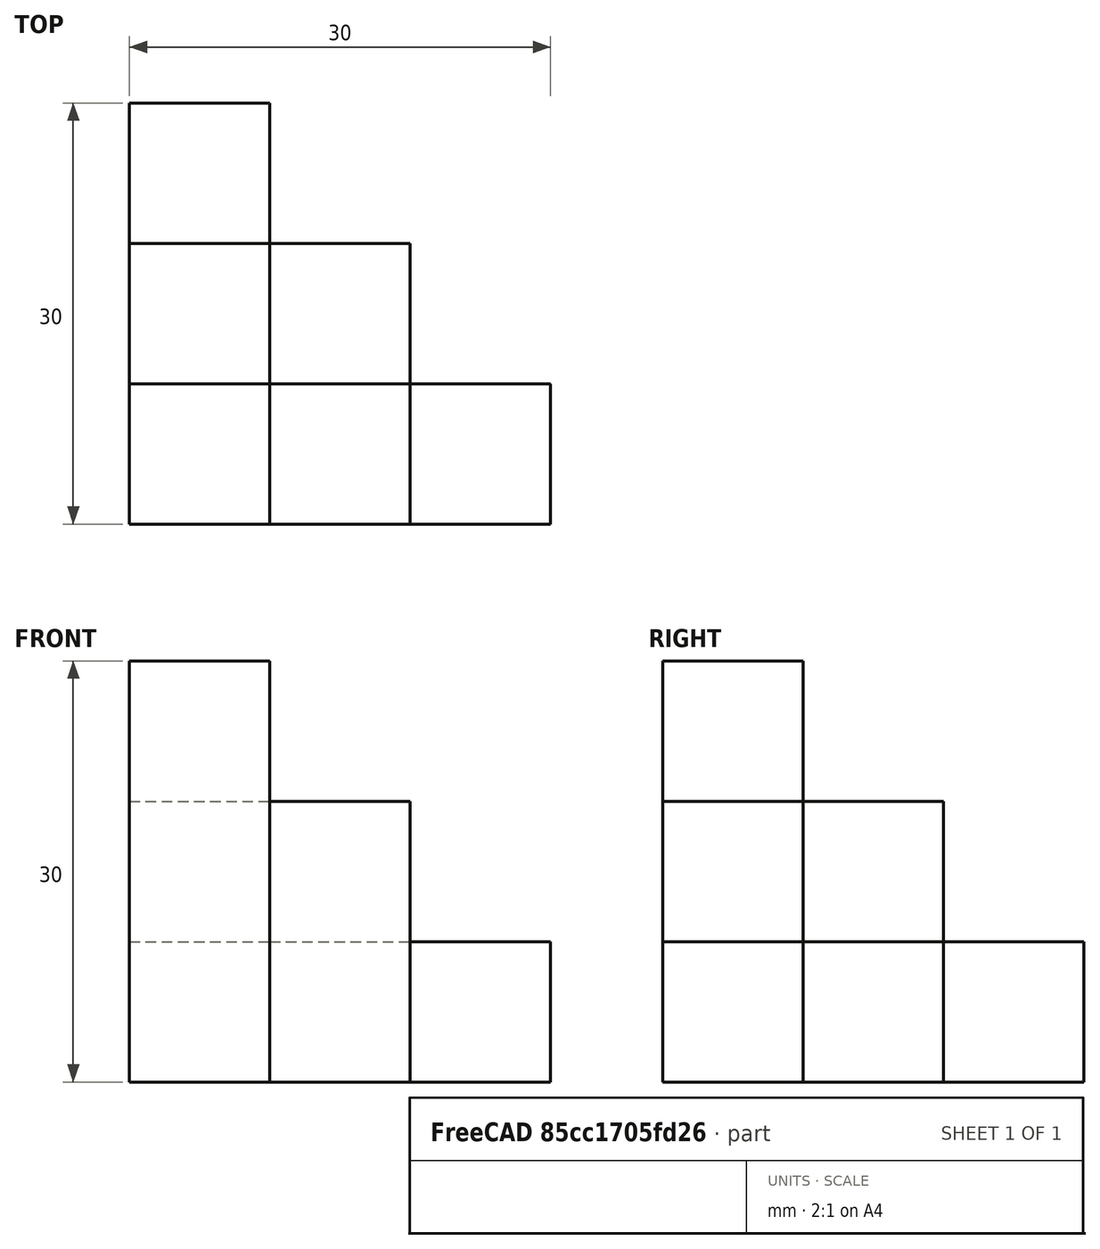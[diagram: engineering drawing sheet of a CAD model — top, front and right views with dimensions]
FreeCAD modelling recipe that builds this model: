
FCSTD DOCUMENT  (FreeCAD 0.21R33694 (Git))
Label: OJT1_T04R03_qubert3
License: All rights reserved
LicenseURL: http://en.wikipedia.org/wiki/All_rights_reserved
objects: Part::Box×6
note: 6 computed .brp shape members not serialized (recipe doc carries the construction recipe); baked Part::Feature solids carry a one-line shape summary decoded from their .brp

FEATURE [Part::Box] Box  label="nivel1-cub1"
  AttacherType = Attacher::AttachEngine3D
  Height = 30
  Length = 10
  Width = 10
FEATURE [Part::Box] Box001  label="nivel2-cub1"
  AttacherType = Attacher::AttachEngine3D
  Height = 20
  Length = 10
  Placement = pos=(10,0,0) rot=(0,0,1;0rad)
  Width = 10
FEATURE [Part::Box] Box002  label="nivel2-cub2"
  AttacherType = Attacher::AttachEngine3D
  Height = 20
  Length = 10
  Placement = pos=(0,10,0) rot=(0,0,1;0rad)
  Width = 10
FEATURE [Part::Box] Box003  label="nivel3-cub1"
  AttacherType = Attacher::AttachEngine3D
  Height = 10
  Length = 10
  Placement = pos=(20,0,0) rot=(0,0,1;0rad)
  Width = 10
FEATURE [Part::Box] Box004  label="nivel3-cub2"
  AttacherType = Attacher::AttachEngine3D
  Height = 10
  Length = 10
  Placement = pos=(0,20,0) rot=(0,0,1;0rad)
  Width = 10
FEATURE [Part::Box] Box005  label="nivel3-cub3"
  AttacherType = Attacher::AttachEngine3D
  Height = 10
  Length = 10
  Placement = pos=(10,10,0) rot=(0,0,1;0rad)
  Width = 10
